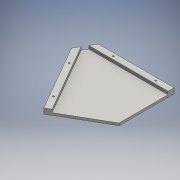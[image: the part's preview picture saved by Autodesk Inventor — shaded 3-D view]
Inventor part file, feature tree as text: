
AUTODESK INVENTOR PART (.ipt)
format: ipt  version: 2016 SP1 (Build 200210100, 210)  size: 135,680 bytes
history: native  units: mm
features: extrude x3, sketch x3, reference x1, projected_geometry x1
ambient origin geometry x8: Origin, YZ Plane, XZ Plane, XY Plane, X Axis, Y Axis, Z Axis, Center Point
bodies: Solid1 (feature_tree)
feature tree (8):
  extrude  "Extrusion1"  Depth=20.0mm
  extrude  "Extrusion2"  Depth=10.0mm
  extrude  "Extrusion3"  Depth=10.0mm
  sketch  "Sketch1"  dims[d0=18.0mm d1=0.0mm d2=20.0mm]
  reference  "Reference1"
  sketch  "Sketch2"  dims[d3=10.0mm d4=0.0mm d5=5.0mm]
  projected_geometry  "Projected Loop1"
  sketch  "Sketch3"  dims[d6=5.0mm d7=5.0mm d8=5.0mm d9=10.0mm d10=10.0mm d11=50.0mm d12=190.0mm d13=10.0mm d14=10.0mm d15=50.0mm d16=190.0mm d17=10.0mm d18=0.0mm]
